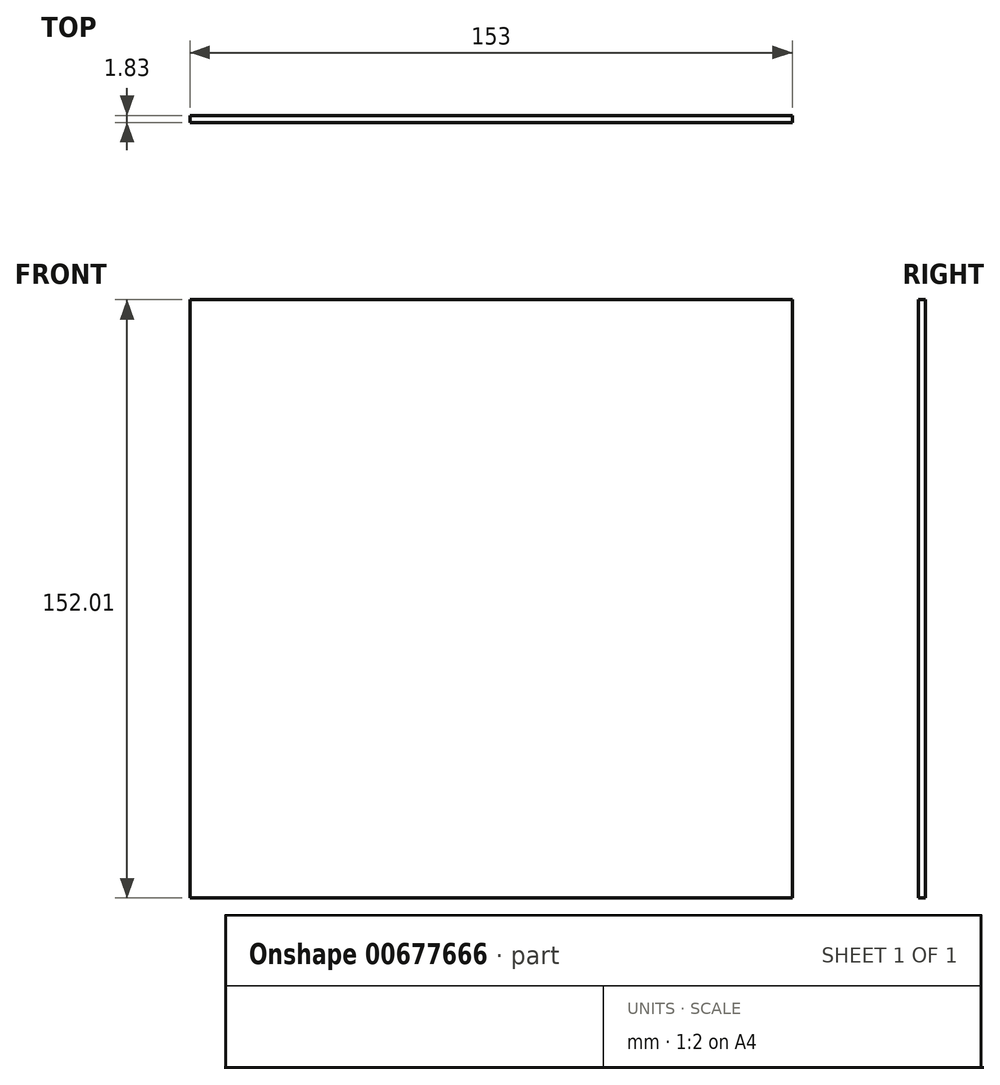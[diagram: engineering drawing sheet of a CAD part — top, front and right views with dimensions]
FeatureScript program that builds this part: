
annotation { "Feature Type Name" : "Feature", "Feature Type Description" : "" }
export const myFeature = defineFeature(function(context is Context, id is Id, definition is map)
    precondition{}
    {
        {
            var Q0;
            Q0=qCreatedBy(makeId("Front.planeOp"),FACE);
            var sketch = newSketch(context, id + "F0", { "sketchPlane" : qUnion([Q0])});
            skLineSegment(sketch, "E0.bottom", {"start": v(-76.75, 76.13) * mm, "end": v(76.25, 76.13) * mm});
            skLineSegment(sketch, "E0.top", {"start": v(-76.75, -75.88) * mm, "end": v(76.25, -75.88) * mm});
            skLineSegment(sketch, "E0.left", {"start": v(-76.75, 76.13) * mm, "end": v(-76.75, -75.88) * mm});
            skLineSegment(sketch, "E0.right", {"start": v(76.25, 76.13) * mm, "end": v(76.25, -75.88) * mm});
            skSolve(sketch);
        }
        {
            var Q0;
            Q0 = qSketchRegion(id + "F0", true);
            extrude(context, id + "F1", {"entities" : qUnion([Q0]), "depth" : 1.83 * mm, "offsetDistance" : 25.4 * mm});
        }
    });
